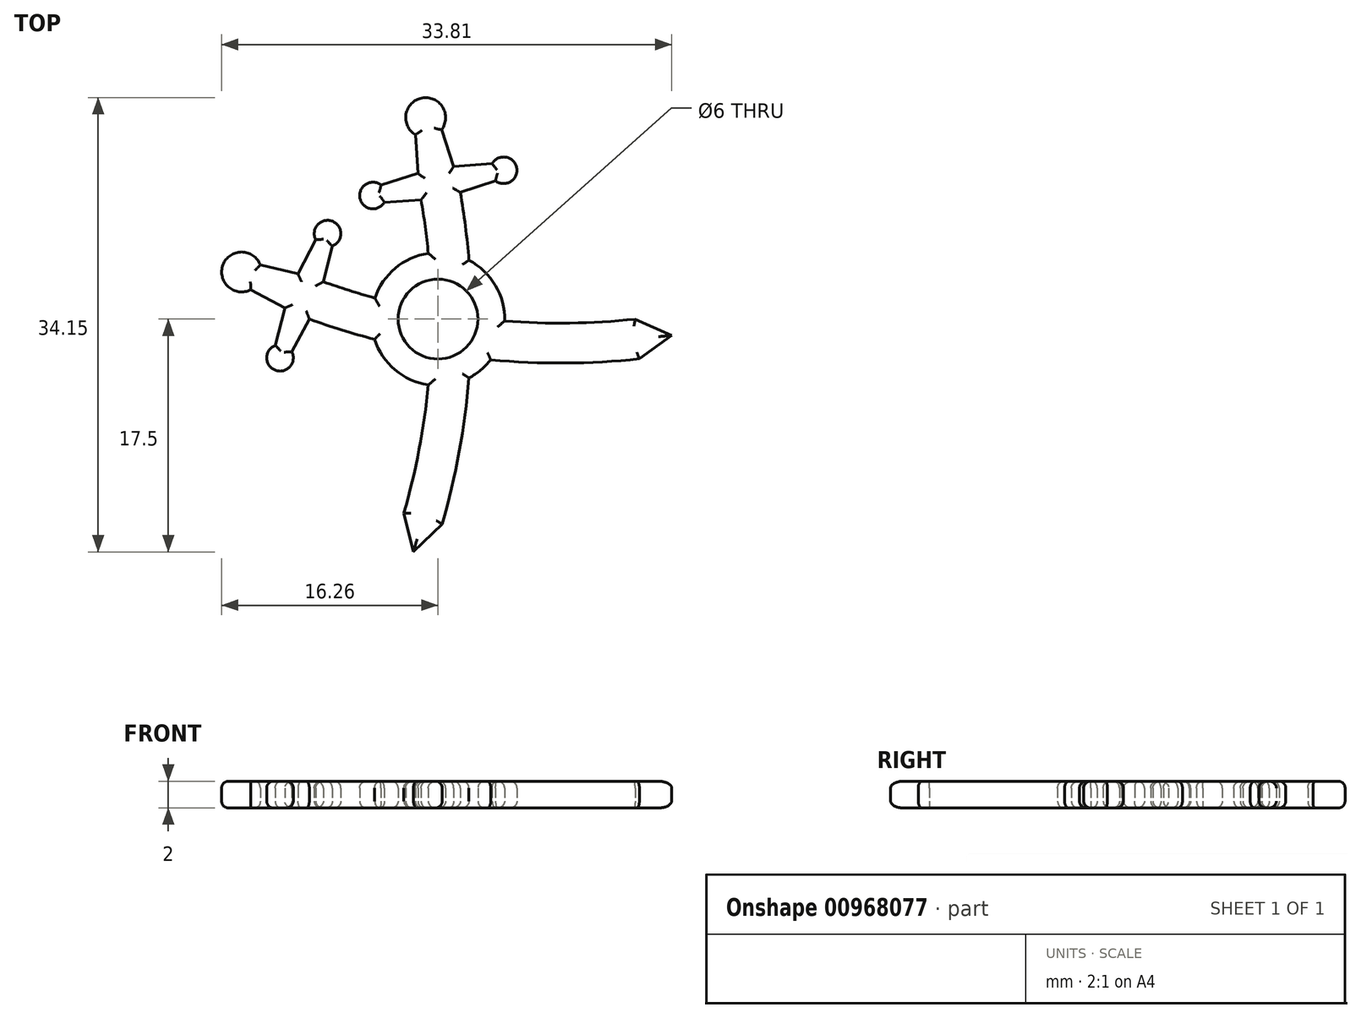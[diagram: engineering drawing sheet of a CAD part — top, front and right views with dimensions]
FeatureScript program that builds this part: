
annotation { "Feature Type Name" : "Feature", "Feature Type Description" : "" }
export const myFeature = defineFeature(function(context is Context, id is Id, definition is map)
    precondition{}
    {
        {
            assignVariable(context, id + "F0", {"name" : "thickness", "anyValue" : 2});
        }
        {
            var Q0;
            Q0=qCreatedBy(makeId("Top.planeOp"),FACE);
            var sketch = newSketch(context, id + "F1", { "sketchPlane" : qUnion([Q0])});
            skArc(sketch, "E0", {"start": v(0, 0) * mm, "mid": v(-0.53, 7.57) * mm, "end": v(-2.13, 15) * mm, "construction": true});
            skArc(sketch, "E1", {"start": v(0, 0) * mm, "mid": v(-0.53, -7.57) * mm, "end": v(-2.13, -15) * mm, "construction": true});
            skArc(sketch, "E2.0", {"start": v(-1.5, 0) * mm, "mid": v(-2.02, -7.36) * mm, "end": v(-3.57, -14.58) * mm});
            skArc(sketch, "E3.0", {"start": v(1.5, 0) * mm, "mid": v(0.95, -7.79) * mm, "end": v(-0.69, -15.42) * mm});
            skLineSegment(sketch, "E4", {"start": v(-2.13, -15) * mm, "end": v(-2.85, -17.5) * mm, "construction": true});
            skLineSegment(sketch, "E5", {"start": v(-2.85, -17.5) * mm, "end": v(-3.57, -14.58) * mm});
            skLineSegment(sketch, "E6", {"start": v(-2.85, -17.5) * mm, "end": v(-0.69, -15.42) * mm});
            skArc(sketch, "E7.0", {"start": v(1.5, 0) * mm, "mid": v(1.25, 5.29) * mm, "end": v(0.5, 10.52) * mm});
            skArc(sketch, "E8.0", {"start": v(-1.5, 0) * mm, "mid": v(-1.74, 5) * mm, "end": v(-2.45, 9.95) * mm});
            skLineSegment(sketch, "E9", {"start": v(-2.45, 9.95) * mm, "end": v(0.5, 10.52) * mm});
            skLineSegment(sketch, "E10", {"start": v(-0.98, 10.24) * mm, "end": v(-1.93, 15.15) * mm, "construction": true});
            skCircle(sketch, "E11", {"center": v(-1.93, 15.15) * mm, "radius": 1.5 * mm});
            skLineSegment(sketch, "E12", {"start": v(-2.45, 9.95) * mm, "end": v(-5.89, 9.3) * mm});
            skLineSegment(sketch, "E13", {"start": v(-5.89, 9.3) * mm, "end": v(0.5, 10.52) * mm, "construction": true});
            skLineSegment(sketch, "E14", {"start": v(0.5, 10.52) * mm, "end": v(3.93, 11.19) * mm, "construction": true});
            skCircle(sketch, "E15", {"center": v(3.93, 11.19) * mm, "radius": 1 * mm});
            skCircle(sketch, "E16", {"center": v(-5.89, 9.3) * mm, "radius": 1 * mm});
            skLineSegment(sketch, "E17", {"start": v(-2.45, 9.95) * mm, "end": v(-2.7, 13.86) * mm});
            skPoint(sketch, "E17.endSnap0", {"position": v(-2.7, 9.9) * mm});
            skLineSegment(sketch, "E18", {"start": v(0.5, 10.52) * mm, "end": v(-0.73, 14.24) * mm});
            skLineSegment(sketch, "E19", {"start": v(3.07, 11.7) * mm, "end": v(0.18, 11.48) * mm});
            skLineSegment(sketch, "E20", {"start": v(3.32, 10.4) * mm, "end": v(0.68, 9.52) * mm});
            skLineSegment(sketch, "E21", {"start": v(-2.52, 10.95) * mm, "end": v(-5.28, 10.09) * mm});
            skLineSegment(sketch, "E22", {"start": v(-5.03, 8.78) * mm, "end": v(-2.27, 8.97) * mm});
            skCircle(sketch, "E23", {"center": v(-1, 0) * mm, "radius": 5 * mm});
            skCircle(sketch, "E24", {"center": v(-1, 0) * mm, "radius": 3 * mm});
            skLineSegment(sketch, "E25", {"start": v(-1, 0) * mm, "end": v(0, 0) * mm, "construction": true});
            skSolve(sketch);
        }
        {
            var Q0;
            Q0=qCreatedBy(makeId("Top.planeOp"),FACE);
            var sketch = newSketch(context, id + "F2", { "sketchPlane" : qUnion([Q0])});
            skLineSegment(sketch, "E26", {"start": v(15.93, 14.2) * mm, "end": v(-17.93, -14.2) * mm, "construction": true});
            skSolve(sketch);
        }
        {
            var Q0;
            Q0=sQuery(id+"F2.wireOp",EDGE,"E26");
            cPlane(context, id + "F3", {"entities" : qUnion([Q0]), "cplaneType" : CPlaneType.MID_PLANE, "offset" : 25 * mm, "width" : 150 * mm, "height" : 150 * mm});
        }
        {
            var Q0;
            Q0 = qSketchRegion(id + "F1", true);
            extrude(context, id + "F4", {"entities" : qUnion([Q0]), "depth" : (getVariable(context, 'thickness')) * mm, "offsetDistance" : 25 * mm});
        }
        {
            var Q0;
            Q0=makeQuery(id+"F4.opExtrude","SWEPT_BODY",BODY,{"disambiguationData":[OSD([sQuery(id+"F1.wireOp",EDGE,"pKbsv3lt-g2ZY-3FcI-WCYi-LG4n8UPdXJOy"),sQuery(id+"F1.wireOp",EDGE,"6h0HU93P-V9k5-Ne0z-rwv7-s9f4UqigbEEF"),sQuery(id+"F1.wireOp",EDGE,"E2.0"),sQuery(id+"F1.wireOp",EDGE,"E3.0"),sQuery(id+"F1.wireOp",EDGE,"E5"),sQuery(id+"F1.wireOp",EDGE,"E6"),sQuery(id+"F1.wireOp",EDGE,"E7.0"),sQuery(id+"F1.wireOp",EDGE,"E8.0"),sQuery(id+"F1.wireOp",EDGE,"E11"),sQuery(id+"F1.wireOp",EDGE,"E15"),sQuery(id+"F1.wireOp",EDGE,"E16"),sQuery(id+"F1.wireOp",EDGE,"E17"),sQuery(id+"F1.wireOp",EDGE,"E18"),sQuery(id+"F1.wireOp",EDGE,"E19"),sQuery(id+"F1.wireOp",EDGE,"E20"),sQuery(id+"F1.wireOp",EDGE,"E21"),sQuery(id+"F1.wireOp",EDGE,"E22")])]});
            var Q1;
            Q1=qCreatedBy(id+"F3.planeOp",FACE);
            mirror(context, id + "F5", {"operationType" : NewBodyOperationType.ADD, "entities" : qUnion([Q0]), "mirrorPlane" : qUnion([Q1])});
        }
        {
            var Q0;
            {var subQ0=makeQuery(id+"F4.opExtrude","CAP_FACE",FACE,{"disambiguationData":[OSD([sQuery(id+"F1.wireOp",EDGE,"pKbsv3lt-g2ZY-3FcI-WCYi-LG4n8UPdXJOy"),sQuery(id+"F1.wireOp",EDGE,"6h0HU93P-V9k5-Ne0z-rwv7-s9f4UqigbEEF"),sQuery(id+"F1.wireOp",EDGE,"E2.0"),sQuery(id+"F1.wireOp",EDGE,"E3.0"),sQuery(id+"F1.wireOp",EDGE,"E5"),sQuery(id+"F1.wireOp",EDGE,"E6"),sQuery(id+"F1.wireOp",EDGE,"E7.0"),sQuery(id+"F1.wireOp",EDGE,"E8.0"),sQuery(id+"F1.wireOp",EDGE,"E11"),sQuery(id+"F1.wireOp",EDGE,"E15"),sQuery(id+"F1.wireOp",EDGE,"E16"),sQuery(id+"F1.wireOp",EDGE,"E17"),sQuery(id+"F1.wireOp",EDGE,"E18"),sQuery(id+"F1.wireOp",EDGE,"E19"),sQuery(id+"F1.wireOp",EDGE,"E20"),sQuery(id+"F1.wireOp",EDGE,"E21"),sQuery(id+"F1.wireOp",EDGE,"E22")])],"isStart":false});Q0=makeQuery(id+"F5.boolean.opBoolean","MERGE",FACE,{"derivedFrom":[subQ0,makeQuery(id+"F5.opPattern","COPY",FACE,{"derivedFrom":subQ0,"instanceName":"1"})]});}
            var Q1;
            {var subQ0=makeQuery(id+"F4.opExtrude","CAP_FACE",FACE,{"disambiguationData":[OSD([sQuery(id+"F1.wireOp",EDGE,"pKbsv3lt-g2ZY-3FcI-WCYi-LG4n8UPdXJOy"),sQuery(id+"F1.wireOp",EDGE,"6h0HU93P-V9k5-Ne0z-rwv7-s9f4UqigbEEF"),sQuery(id+"F1.wireOp",EDGE,"E2.0"),sQuery(id+"F1.wireOp",EDGE,"E3.0"),sQuery(id+"F1.wireOp",EDGE,"E5"),sQuery(id+"F1.wireOp",EDGE,"E6"),sQuery(id+"F1.wireOp",EDGE,"E7.0"),sQuery(id+"F1.wireOp",EDGE,"E8.0"),sQuery(id+"F1.wireOp",EDGE,"E11"),sQuery(id+"F1.wireOp",EDGE,"E15"),sQuery(id+"F1.wireOp",EDGE,"E16"),sQuery(id+"F1.wireOp",EDGE,"E17"),sQuery(id+"F1.wireOp",EDGE,"E18"),sQuery(id+"F1.wireOp",EDGE,"E19"),sQuery(id+"F1.wireOp",EDGE,"E20"),sQuery(id+"F1.wireOp",EDGE,"E21"),sQuery(id+"F1.wireOp",EDGE,"E22")])],"isStart":true});Q1=makeQuery(id+"F5.boolean.opBoolean","MERGE",FACE,{"derivedFrom":[subQ0,makeQuery(id+"F5.opPattern","COPY",FACE,{"derivedFrom":subQ0,"instanceName":"1"})]});}
            fillet(context, id + "F6", {"entities" : qUnion([Q0, Q1]), "radius" : (getVariable(context, 'thickness') / 4) * mm, "tangentPropagation" : true, "allowEdgeOverflow" : false});
        }
    });
